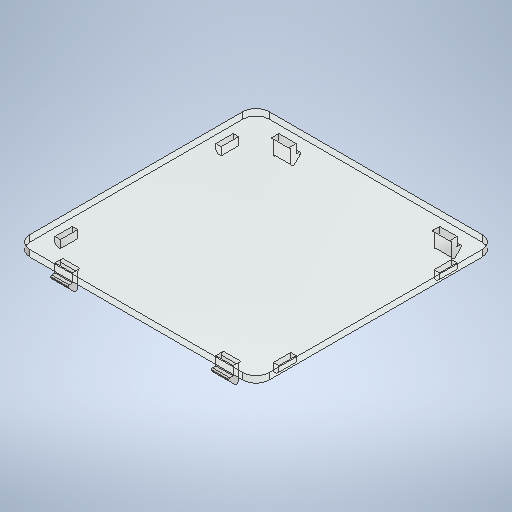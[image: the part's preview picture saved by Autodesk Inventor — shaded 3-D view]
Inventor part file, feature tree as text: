
AUTODESK INVENTOR PART (.ipt)
format: ipt  version: 2025 (Build 290162000, 162)  size: 403,456 bytes
history: native  units: mm
features: fillet x7, sketch x7, extrude x5, chamfer x3, other x1
ambient origin geometry x8: Origin, YZ Plane, XZ Plane, XY Plane, X Axis, Y Axis, Z Axis, Center Point
bodies: Solid1 (feature_tree)
feature tree (23):
  extrude  "Extrusion1"  Depth=110.0mm
  fillet  "Fillet1"  Radius=6.0mm
  extrude  "Extrusion3"  Depth=6.0mm
  extrude  "Extrusion4"  Depth=2.5mm
  chamfer  "Chamfer1"  Distance=74.0mm
  fillet  "Fillet2"  Radius=100.5mm
  fillet  "Fillet3"  Radius=8.1mm
  extrude  "Extrusion5"  TaperAngle=0.0deg  [1 undecoded]
  chamfer  "Chamfer2"  Distance=4.0mm
  fillet  "Fillet4"  Radius=2.0mm
  fillet  "Fillet5"  Radius=3.0mm
  fillet  "Fillet6"  Radius=1.0mm
  fillet  "Fillet7"  Radius=0.5mm
  extrude  "Extrusion6"  Depth=4.05mm
  chamfer  "Chamfer3"  Distance=2.0mm
  sketch  "Sketch1"  dims[d0=110.0mm d1=110.0mm d2=6.0mm]
  sketch  "Sketch3"  dims[d22=3.5mm]
  sketch  "Sketch Rectangular Pattern1"  dims[d3=3.0mm d4=0.0mm d5=6.0mm]
  sketch  "Sketch4"  dims[d23=14.0mm d24=20.0mm d26=74.0mm d27=20.0mm d29=100.5mm d32=8.1mm d33=0.0mm]
  sketch  "Sketch5"  dims[d34=4.0mm d35=0.0mm]
  sketch  "Sketch Rectangular Pattern2"  dims[d20=8.0mm d21=2.5mm]
  sketch  "Sketch6"  dims[d36=0.0mm d37=4.0mm d38=2.0mm d39=0.0mm d40=3.0mm d41=2.0mm d42=45.0deg d43=1.0mm d44=0.5mm d45=4.05mm d46=2.0mm d47=0.0mm d48=3.0mm d49=2.0mm d50=45.0deg d51=1.0mm d52=0.5mm d53=1.0mm d54=1.0mm d55=8.0mm d56=2.5mm d57=14.0mm d58=20.0mm d60=74.0mm d61=20.0mm d63=100.5mm d66=3.5mm d67=4.5mm d68=0.0mm d69=1.0mm d70=2.0mm d71=45.0deg]
  other  "Finish1"
note: 1 required parameter value undecoded (feature->parameter linkage not recoverable at this tier; creation-order binding heuristic only, values carry confidence <= 0.55)
